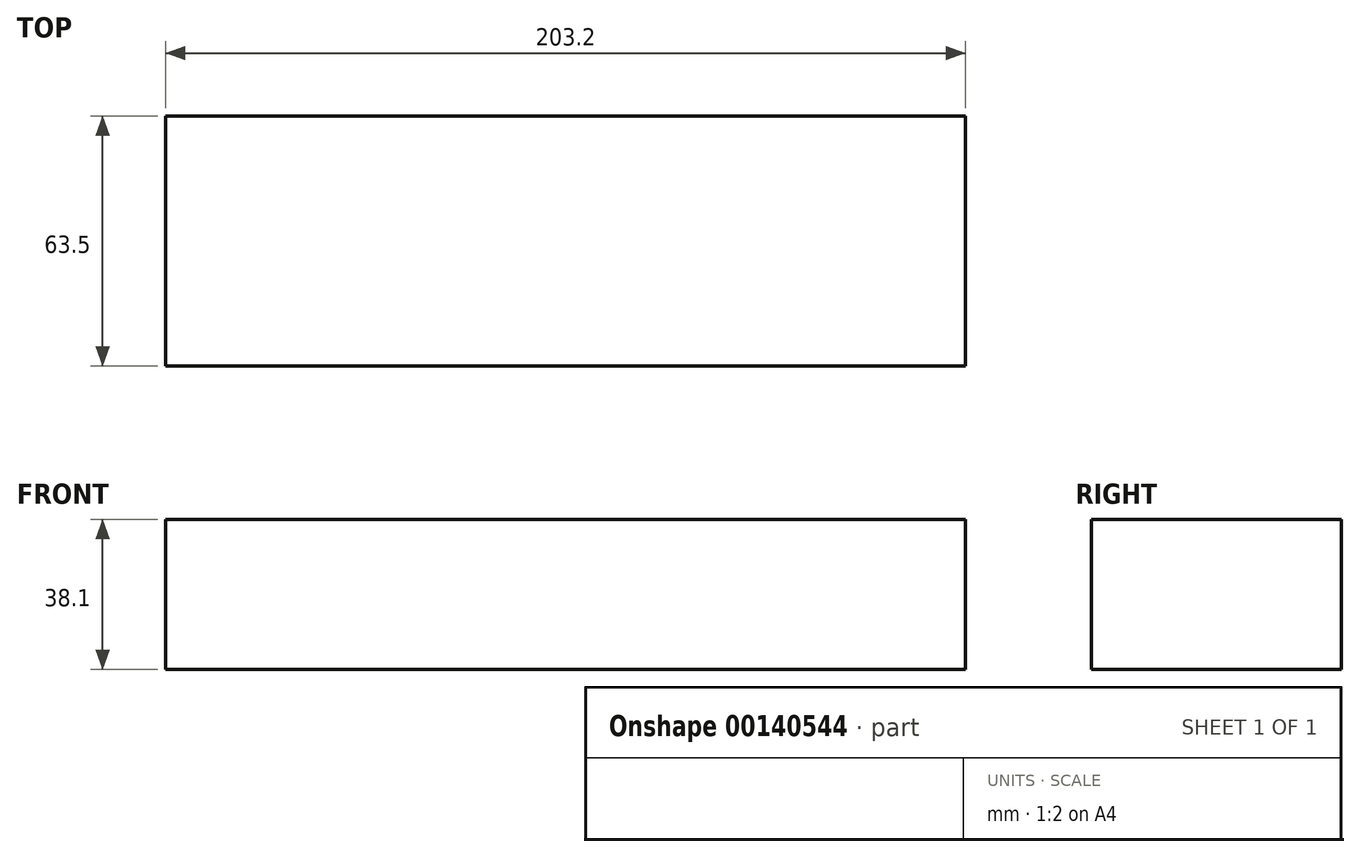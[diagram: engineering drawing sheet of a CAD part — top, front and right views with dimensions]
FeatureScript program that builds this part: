
annotation { "Feature Type Name" : "Feature", "Feature Type Description" : "" }
export const myFeature = defineFeature(function(context is Context, id is Id, definition is map)
    precondition{}
    {
        {
            var Q0;
            Q0=qCreatedBy(makeId("Top.planeOp"),FACE);
            var sketch = newSketch(context, id + "F1", { "sketchPlane" : qUnion([Q0])});
            skLineSegment(sketch, "E0.bottom", {"start": v(0, 0) * mm, "end": v(203.2, 0) * mm});
            skLineSegment(sketch, "E0.top", {"start": v(0, 63.5) * mm, "end": v(203.2, 63.5) * mm});
            skLineSegment(sketch, "E0.left", {"start": v(0, 0) * mm, "end": v(0, 63.5) * mm});
            skLineSegment(sketch, "E0.right", {"start": v(203.2, 0) * mm, "end": v(203.2, 63.5) * mm});
            skSolve(sketch);
        }
        {
            var Q0;
            Q0 = qSketchRegion(id + "F1", true);
            extrude(context, id + "F0", {"entities" : qUnion([Q0]), "depth" : 38.1 * mm});
        }
    });
